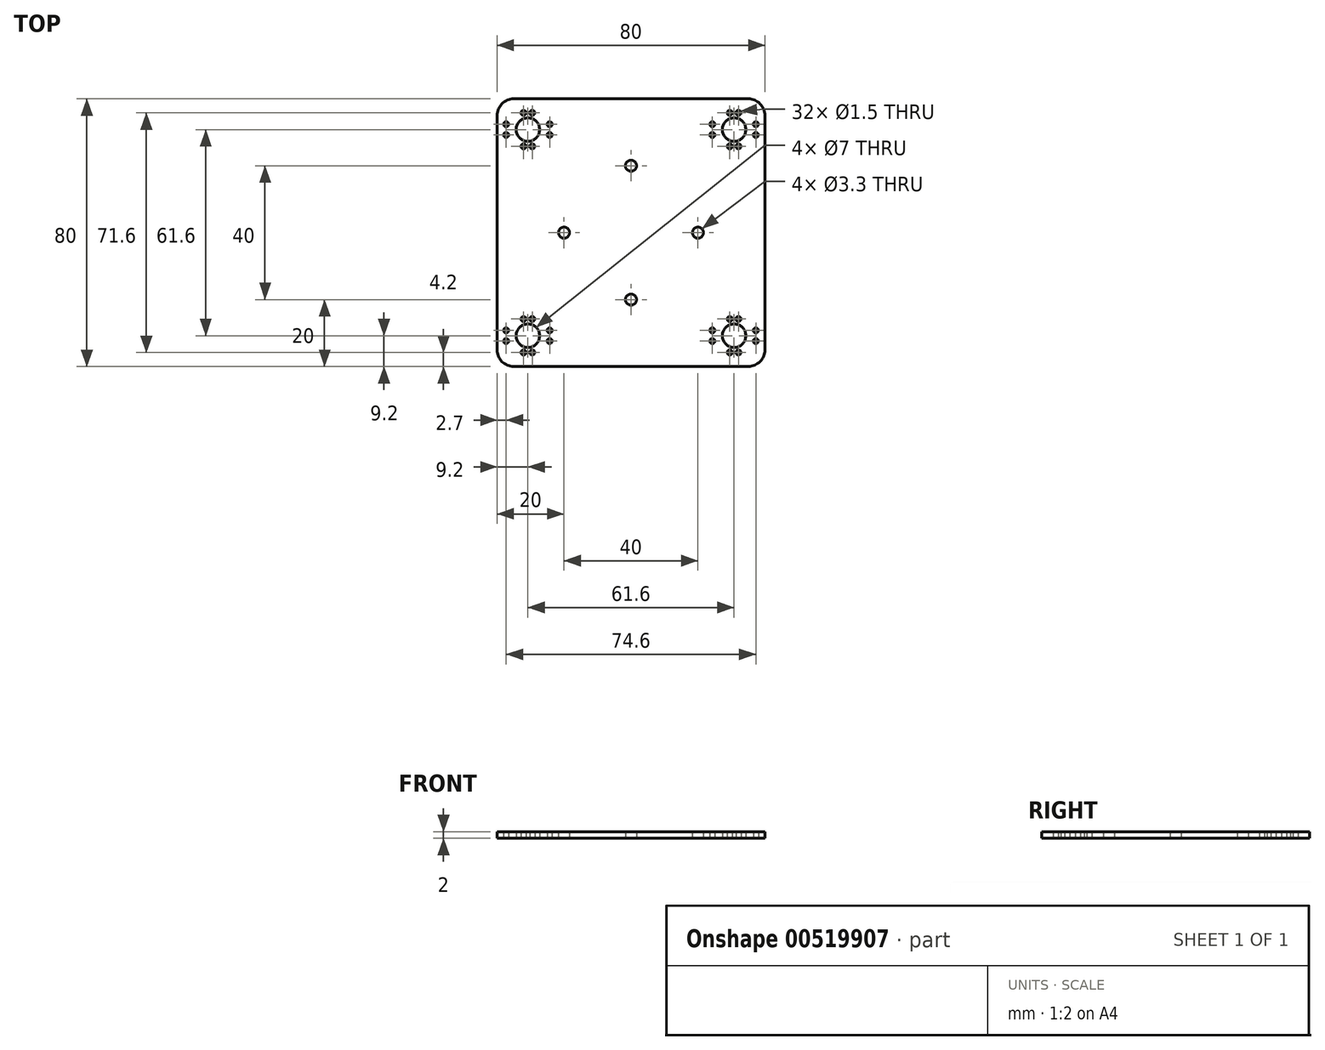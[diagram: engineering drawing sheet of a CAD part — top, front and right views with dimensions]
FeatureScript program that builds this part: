
annotation { "Feature Type Name" : "Feature", "Feature Type Description" : "" }
export const myFeature = defineFeature(function(context is Context, id is Id, definition is map)
    precondition{}
    {
        {
            var Q0;
            Q0=qCreatedBy(makeId("Top.planeOp"),FACE);
            var sketch = newSketch(context, id + "F0", { "sketchPlane" : qUnion([Q0])});
            skLineSegment(sketch, "E0", {"start": v(0, 0) * mm, "end": v(40, 0) * mm, "construction": true});
            skLineSegment(sketch, "E1", {"start": v(40, 0) * mm, "end": v(40, -40) * mm, "construction": true});
            skLineSegment(sketch, "E2", {"start": v(35, -40) * mm, "end": v(-35, -40) * mm});
            skLineSegment(sketch, "E3", {"start": v(-40, -35) * mm, "end": v(-40, 35) * mm});
            skLineSegment(sketch, "E4", {"start": v(-35, 40) * mm, "end": v(35, 40) * mm});
            skLineSegment(sketch, "E5", {"start": v(40, 35) * mm, "end": v(40, -35) * mm});
            skLineSegment(sketch, "E6", {"start": v(40, -40) * mm, "end": v(30.8, -40) * mm, "construction": true});
            skLineSegment(sketch, "E7", {"start": v(30.8, -40) * mm, "end": v(30.8, -30.8) * mm, "construction": true});
            skCircle(sketch, "E8", {"center": v(30.8, -30.8) * mm, "radius": 3.5 * mm});
            skLineSegment(sketch, "E9", {"start": v(30.8, -30.8) * mm, "end": v(37.3, -30.8) * mm, "construction": true});
            skLineSegment(sketch, "E10", {"start": v(37.3, -30.8) * mm, "end": v(37.3, -32.4) * mm, "construction": true});
            skCircle(sketch, "E11", {"center": v(37.3, -32.4) * mm, "radius": 0.75 * mm});
            skLineSegment(sketch, "E12", {"start": v(30.8, -30.8) * mm, "end": v(30.8, -35.8) * mm, "construction": true});
            skLineSegment(sketch, "E13", {"start": v(30.8, -35.8) * mm, "end": v(32.1, -35.8) * mm, "construction": true});
            skCircle(sketch, "E14", {"center": v(32.1, -35.8) * mm, "radius": 0.75 * mm});
            skCircle(sketch, "E15.MirrorC", {"center": v(29.5, -35.8) * mm, "radius": 0.75 * mm});
            skCircle(sketch, "E16.MirrorC", {"center": v(24.3, -32.4) * mm, "radius": 0.75 * mm});
            skCircle(sketch, "E17.MirrorC", {"center": v(37.3, -29.2) * mm, "radius": 0.75 * mm});
            skCircle(sketch, "E18.MirrorC", {"center": v(24.3, -29.2) * mm, "radius": 0.75 * mm});
            skCircle(sketch, "E19.MirrorC", {"center": v(32.1, -25.8) * mm, "radius": 0.75 * mm});
            skCircle(sketch, "E20.MirrorC", {"center": v(29.5, -25.8) * mm, "radius": 0.75 * mm});
            skLineSegment(sketch, "E21.MirrorCS", {"start": v(30.8, 35.8) * mm, "end": v(32.1, 35.8) * mm, "construction": true});
            skCircle(sketch, "E22.MirrorC", {"center": v(29.5, 35.8) * mm, "radius": 0.75 * mm});
            skLineSegment(sketch, "E23.MirrorCS", {"start": v(30.8, 30.8) * mm, "end": v(30.8, 35.8) * mm, "construction": true});
            skLineSegment(sketch, "E24.MirrorCS", {"start": v(30.8, 30.8) * mm, "end": v(37.3, 30.8) * mm, "construction": true});
            skLineSegment(sketch, "E25.MirrorCS", {"start": v(37.3, 30.8) * mm, "end": v(37.3, 32.4) * mm, "construction": true});
            skCircle(sketch, "E26.MirrorC", {"center": v(32.1, 35.8) * mm, "radius": 0.75 * mm});
            skCircle(sketch, "E27.MirrorC", {"center": v(24.3, 29.2) * mm, "radius": 0.75 * mm});
            skCircle(sketch, "E28.MirrorC", {"center": v(30.8, 30.8) * mm, "radius": 3.5 * mm});
            skCircle(sketch, "E29.MirrorC", {"center": v(29.5, 25.8) * mm, "radius": 0.75 * mm});
            skCircle(sketch, "E30.MirrorC", {"center": v(24.3, 32.4) * mm, "radius": 0.75 * mm});
            skCircle(sketch, "E31.MirrorC", {"center": v(32.1, 25.8) * mm, "radius": 0.75 * mm});
            skCircle(sketch, "E32.MirrorC", {"center": v(37.3, 29.2) * mm, "radius": 0.75 * mm});
            skCircle(sketch, "E33.MirrorC", {"center": v(37.3, 32.4) * mm, "radius": 0.75 * mm});
            skCircle(sketch, "E34.MirrorC", {"center": v(-24.3, 32.4) * mm, "radius": 0.75 * mm});
            skCircle(sketch, "E35.MirrorC", {"center": v(-24.3, 29.2) * mm, "radius": 0.75 * mm});
            skLineSegment(sketch, "E36.MirrorCS", {"start": v(-30.8, 35.8) * mm, "end": v(-32.1, 35.8) * mm, "construction": true});
            skCircle(sketch, "E37.MirrorC", {"center": v(-29.5, 25.8) * mm, "radius": 0.75 * mm});
            skCircle(sketch, "E38.MirrorC", {"center": v(-29.5, 35.8) * mm, "radius": 0.75 * mm});
            skCircle(sketch, "E39.MirrorC", {"center": v(-37.3, 32.4) * mm, "radius": 0.75 * mm});
            skCircle(sketch, "E40.MirrorC", {"center": v(-32.1, 35.8) * mm, "radius": 0.75 * mm});
            skLineSegment(sketch, "E41.MirrorCS", {"start": v(-30.8, 30.8) * mm, "end": v(-37.3, 30.8) * mm, "construction": true});
            skCircle(sketch, "E42.MirrorC", {"center": v(-32.1, 25.8) * mm, "radius": 0.75 * mm});
            skLineSegment(sketch, "E43.MirrorCS", {"start": v(-30.8, 30.8) * mm, "end": v(-30.8, 35.8) * mm, "construction": true});
            skLineSegment(sketch, "E44.MirrorCS", {"start": v(-37.3, 30.8) * mm, "end": v(-37.3, 32.4) * mm, "construction": true});
            skCircle(sketch, "E45.MirrorC", {"center": v(-37.3, 29.2) * mm, "radius": 0.75 * mm});
            skCircle(sketch, "E46.MirrorC", {"center": v(-30.8, 30.8) * mm, "radius": 3.5 * mm});
            skCircle(sketch, "E47.MirrorC", {"center": v(-29.5, -35.8) * mm, "radius": 0.75 * mm});
            skLineSegment(sketch, "E48.MirrorCS", {"start": v(-30.8, -30.8) * mm, "end": v(-30.8, -35.8) * mm, "construction": true});
            skLineSegment(sketch, "E49.MirrorCS", {"start": v(-30.8, -30.8) * mm, "end": v(-37.3, -30.8) * mm, "construction": true});
            skCircle(sketch, "E50.MirrorC", {"center": v(-32.1, -35.8) * mm, "radius": 0.75 * mm});
            skCircle(sketch, "E51.MirrorC", {"center": v(-37.3, -32.4) * mm, "radius": 0.75 * mm});
            skCircle(sketch, "E52.MirrorC", {"center": v(-24.3, -29.2) * mm, "radius": 0.75 * mm});
            skLineSegment(sketch, "E53.MirrorCS", {"start": v(-30.8, -35.8) * mm, "end": v(-32.1, -35.8) * mm, "construction": true});
            skCircle(sketch, "E54.MirrorC", {"center": v(-37.3, -29.2) * mm, "radius": 0.75 * mm});
            skLineSegment(sketch, "E55.MirrorCS", {"start": v(-37.3, -30.8) * mm, "end": v(-37.3, -32.4) * mm, "construction": true});
            skCircle(sketch, "E56.MirrorC", {"center": v(-24.3, -32.4) * mm, "radius": 0.75 * mm});
            skCircle(sketch, "E57.MirrorC", {"center": v(-32.1, -25.8) * mm, "radius": 0.75 * mm});
            skCircle(sketch, "E58.MirrorC", {"center": v(-30.8, -30.8) * mm, "radius": 3.5 * mm});
            skCircle(sketch, "E59.MirrorC", {"center": v(-29.5, -25.8) * mm, "radius": 0.75 * mm});
            skPoint(sketch, "E60.visualSharp", {"position": v(-40, 40) * mm});
            skArc(sketch, "E60.filletArc", {"start": v(-35, 40) * mm, "mid": v(-38.54, 38.54) * mm, "end": v(-40, 35) * mm});
            skPoint(sketch, "E61.visualSharp", {"position": v(40, 40) * mm});
            skArc(sketch, "E61.filletArc", {"start": v(40, 35) * mm, "mid": v(38.54, 38.54) * mm, "end": v(35, 40) * mm});
            skPoint(sketch, "E62.visualSharp", {"position": v(40, -40) * mm});
            skArc(sketch, "E62.filletArc", {"start": v(35, -40) * mm, "mid": v(38.54, -38.54) * mm, "end": v(40, -35) * mm});
            skPoint(sketch, "E63.visualSharp", {"position": v(-40, -40) * mm});
            skArc(sketch, "E63.filletArc", {"start": v(-40, -35) * mm, "mid": v(-38.54, -38.54) * mm, "end": v(-35, -40) * mm});
            skLineSegment(sketch, "E64", {"start": v(30.8, 30.8) * mm, "end": v(30.8, -30.8) * mm, "construction": true});
            skLineSegment(sketch, "E65", {"start": v(-30.8, 30.8) * mm, "end": v(30.8, 30.8) * mm, "construction": true});
            skLineSegment(sketch, "E66", {"start": v(40, 0) * mm, "end": v(20, 0) * mm, "construction": true});
            skCircle(sketch, "E67", {"center": v(20, 0) * mm, "radius": 1.65 * mm});
            skCircle(sketch, "E68.MirrorC", {"center": v(-20, 0) * mm, "radius": 1.65 * mm});
            skLineSegment(sketch, "E69", {"start": v(0, -40) * mm, "end": v(0, -20) * mm, "construction": true});
            skCircle(sketch, "E70", {"center": v(0, -20) * mm, "radius": 1.65 * mm});
            skCircle(sketch, "E71.MirrorC", {"center": v(0, 20) * mm, "radius": 1.65 * mm});
            skSolve(sketch);
        }
        {
            var Q0;
            Q0=makeQuery(id+"F0.imprint","IMPRINT",FACE,{"disambiguationData":[TD([[makeQuery(id+"F0.imprint","IMPRINT",EDGE,{"derivedFrom":sQuery(id+"F0.wireOp",EDGE,"E2")}),-1.0]])]});
            extrude(context, id + "F1", {"entities" : qUnion([Q0]), "depth" : 2 * mm, "offsetDistance" : 25 * mm});
        }
    });
